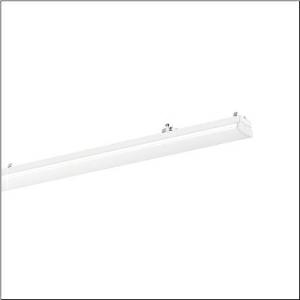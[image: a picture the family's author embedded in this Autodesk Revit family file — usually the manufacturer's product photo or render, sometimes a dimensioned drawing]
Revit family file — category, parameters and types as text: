
# Revit family: licross_r__11_recessed_opal_mo_51tl1ddn445g_7b5e
name_source: partatom
category: Lighting Fixtures
units: mm (PartAtom-declared; Revit-internal decimal feet)

## family parameters
Cut with Voids When Loaded = No
Host = Face
Light Source = No
Part Type = Normal
Room Calculation Point = No
Round Connector Dimension = Use Diameter
Shared = No

## types (1)
- --- (1 x LED, 4500 lm, 25.2 W, 4000K)
    Apparent Load = 25 VA
    CIE Flux Codes = 44 73 91 87 100
    Color Rendering = 80
    Color Temperature = 4000K
    Default Elevation = 1800 mm
    Description = Licross® 11 recessed opal MO, luminaire insert, of sheet steel, coil coated, white, length: 1.500mm, width: 76mm, height: 87mm, LED rated luminous flux: 4.500lm, light colour: 840, control gear: DALI 2, with plug, 5-pole, with phase selection, mains connection: 220..240V, AC, 50/60Hz, rated input power: 25W, halogen-free wiring, primary optical cover: cover, of PMMA, light emission: direct with ceiling illumination distribution, primary light characteristic: symmetric, protection rating (complete): IP40, insulation class (complete): insulation class I (protective earthing), certification: CE, ENEC, VDE, UKCA, protection symbol: D if used in an environment without relevant dust loads with corresponding accessories, impact resistance: IK06, permissible ambient temperature for indoor applications: -25..+45°C, corresponds to IFS (International Featured Standards) requirements for safety and quality in the food industry, reducing of maximum allowable ambient temperature of 5°C with ceiling mounting, LABS conformity tested according to VDMA 24364:2018-05, packaging unit: 1 piece
    Height = 83 mm
    Lamp = 1 x LED
    Lamp Light Flux = 4500 lm
    Lamp Power = 25.2 W
    Lamp count = 1
    Length = 1500 mm
    Luminous efficacy = 179 lm/W
    Manufacturer = Siteco
    ModVariant = No
    Model = 51TL1DDN445G
    Mounting Place = Ceiling
    Mounting Type = Pendant
    Number of Poles = 1
    OnlyDefault = Yes
    Power Factor = 1
    Product Name = Licross® 11 recessed opal MO
    Product group = luminaire insert
    ProductGroupID = 902
    Protection Class = Protection class I
    Protection Degree = IP 40
    RLX_Detail_Level = 1
    RLX_Emergency_Light_Flux = 0 lm
    RLX_Emergency_Type = 0
    RLX_Emergency_Type_DB = No
    RlxData = <blob elided: 26653 chars, md5=388f4c3a>
    Socket = socket
    Standby Power = 0 W
    System Light Flux = 4500 lm
    System Power = 25 W
    Type Comments = factory setting: luminous flux: 100 % | dim-lin: 254 | 167 mA
    Type Image = l_1313666.jpg
    URL = http://relux.com
    VarID = @adj_076230
    Voltage = 0 V
    Weight = 0.00 kg
    Width = 76 mm

## geometry (parser evidence)
native form markers: Blend x4, Sweep x12
no freeform markers — native parametric forms only
